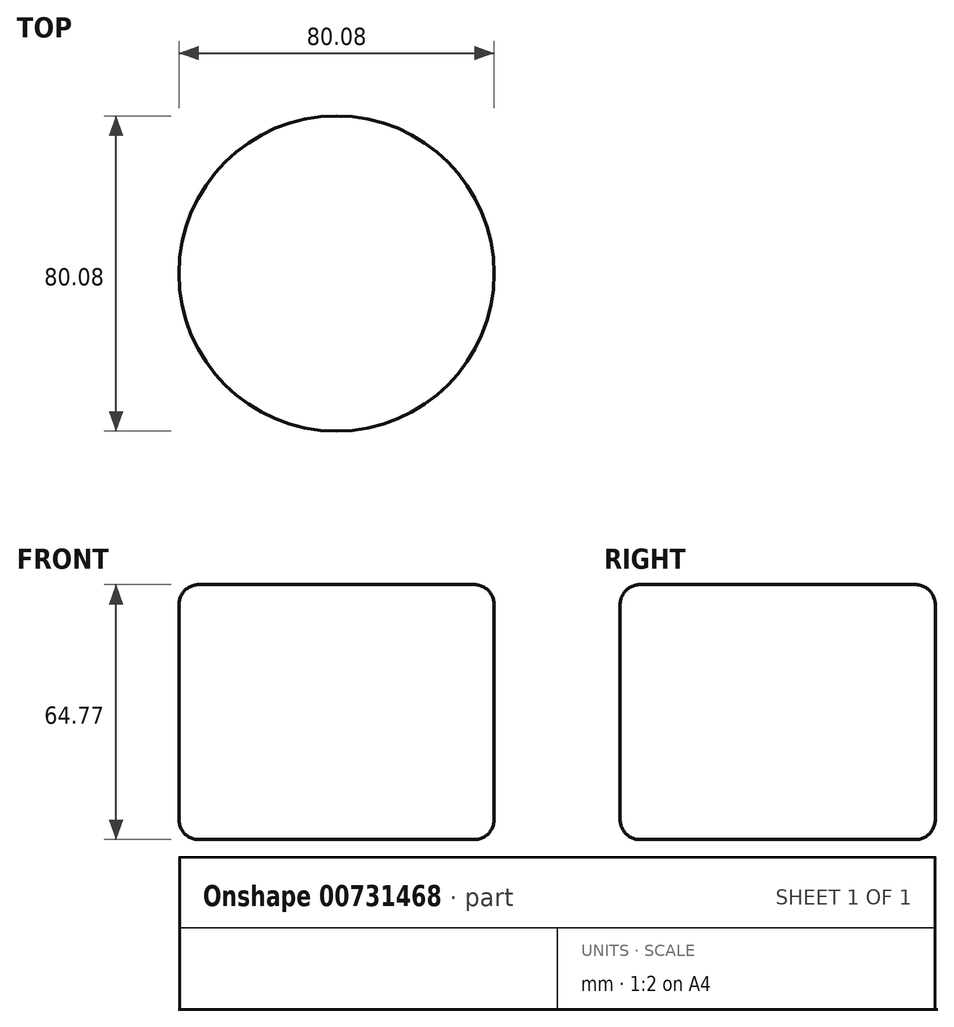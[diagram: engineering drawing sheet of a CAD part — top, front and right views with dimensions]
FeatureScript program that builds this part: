
annotation { "Feature Type Name" : "Feature", "Feature Type Description" : "" }
export const myFeature = defineFeature(function(context is Context, id is Id, definition is map)
    precondition{}
    {
        {
            var Q0;
            Q0=qCreatedBy(makeId("Top.planeOp"),FACE);
            var sketch = newSketch(context, id + "F0", { "sketchPlane" : qUnion([Q0])});
            skCircle(sketch, "E0", {"center": v(0, 0) * mm, "radius": 40.04 * mm});
            skCircle(sketch, "E1", {"center": v(0, 0) * mm, "radius": 20.1 * mm});
            skSolve(sketch);
        }
        {
            var Q0;
            Q0=makeQuery(id+"F0.imprint","IMPRINT",FACE,{"disambiguationData":[TD([[makeQuery(id+"F0.imprint","IMPRINT",EDGE,{"derivedFrom":sQuery(id+"F0.wireOp",EDGE,"E1")}),1.0]])]});
            var Q1;
            Q1=makeQuery(id+"F0.imprint","IMPRINT",FACE,{"disambiguationData":[TD([[makeQuery(id+"F0.imprint","IMPRINT",EDGE,{"derivedFrom":sQuery(id+"F0.wireOp",EDGE,"E0")}),1.0]])]});
            extrude(context, id + "F1", {"entities" : qUnion([Q0, Q1]), "oppositeDirection" : true, "depth" : 64.77 * mm, "offsetDistance" : 25.4 * mm});
        }
        {
            var Q0;
            Q0=makeQuery(id+"F1.opExtrude","CAP_FACE",FACE,{"disambiguationData":[OSD([sQuery(id+"F0.wireOp",EDGE,"E0")])],"isStart":true});
            var sketch = newSketch(context, id + "F2", { "sketchPlane" : qUnion([Q0])});
            skCircle(sketch, "E2", {"center": v(0, 0) * mm, "radius": 24.48 * mm});
            skSolve(sketch);
        }
        {
            var Q0;
            Q0=sQuery(id+"F2.wireOp",EDGE,"E2");
            extrude(context, id + "F3", {"bodyType" : ToolBodyType.SURFACE, "surfaceEntities" : qUnion([Q0]), "depth" : 63.5 * mm, "offsetDistance" : 25.4 * mm});
        }
        {
            var Q0;
            Q0=makeQuery(id+"F1.opExtrude","CAP_FACE",FACE,{"disambiguationData":[OSD([sQuery(id+"F0.wireOp",EDGE,"E0")])],"isStart":true});
            var sketch = newSketch(context, id + "F4", { "sketchPlane" : qUnion([Q0])});
            skCircle(sketch, "E3", {"center": v(0, 0) * mm, "radius": 11.48 * mm});
            skSolve(sketch);
        }
        {
            var Q0;
            Q0=makeQuery(id+"F4.imprint","IMPRINT",FACE,{"disambiguationData":[TD([[makeQuery(id+"F4.imprint","IMPRINT",EDGE,{"derivedFrom":sQuery(id+"F4.wireOp",EDGE,"E3")}),1.0]])]});
            var Q1;
            Q1=sQuery(id+"F4.wireOp",EDGE,"E3");
            extrude(context, id + "F5", {"entities" : qUnion([Q0]), "bodyType" : ToolBodyType.SURFACE, "operationType" : NewBodyOperationType.REMOVE, "surfaceEntities" : qUnion([Q1]), "depth" : 120.4 * mm, "offsetDistance" : 25.4 * mm});
        }
        {
            var Q0;
            Q0=makeQuery(id+"F1.opExtrude","SWEPT_FACE",FACE,{"disambiguationData":[OSD([sQuery(id+"F0.wireOp",EDGE,"E0")])]});
            fillet(context, id + "F6", {"entities" : qUnion([Q0]), "radius" : 5.08 * mm, "tangentPropagation" : true, "allowEdgeOverflow" : false});
        }
        {
            var Q0;
            Q0=makeQuery(id+"F1.opExtrude","CAP_FACE",FACE,{"disambiguationData":[OSD([sQuery(id+"F0.wireOp",EDGE,"E0")])],"isStart":false});
            var sketch = newSketch(context, id + "F7", { "sketchPlane" : qUnion([Q0])});
            skCircle(sketch, "E4", {"center": v(-12.36, 16.27) * mm, "radius": 6.57 * mm});
            skCircle(sketch, "E5.1.0", {"center": v(-7.91, -18.84) * mm, "radius": 6.57 * mm});
            skCircle(sketch, "E5.2.0", {"center": v(20.27, 2.57) * mm, "radius": 6.57 * mm});
            skPoint(sketch, "E5.center", {"position": v(0, 0) * mm});
            skSolve(sketch);
        }
        {
            var Q0;
            Q0=sQuery(id+"F7.wireOp",EDGE,"E4");
            var Q1;
            Q1=sQuery(id+"F7.wireOp",EDGE,"E5.1.0");
            var Q2;
            Q2=sQuery(id+"F7.wireOp",EDGE,"E5.2.0");
            extrude(context, id + "F8", {"bodyType" : ToolBodyType.SURFACE, "surfaceEntities" : qUnion([Q0, Q1, Q2]), "depth" : 97.03 * mm, "offsetDistance" : 25.4 * mm});
        }
    });
